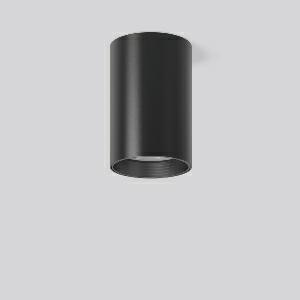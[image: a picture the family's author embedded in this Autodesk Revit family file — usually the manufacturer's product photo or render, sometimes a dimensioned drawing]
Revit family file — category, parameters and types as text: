
# Revit family: heledon_maxi_a_931229_003_1_3319
name_source: partatom
category: Lighting Fixtures
units: mm (PartAtom-declared; Revit-internal decimal feet)

## family parameters
Cut with Voids When Loaded = No
Host = Face
Light Source = No
Part Type = Normal
Room Calculation Point = No
Round Connector Dimension = Use Diameter
Shared = No

## types (1)
- HELEDON maxi A (1 x LED Modul 940, 3800 lm, 4000)
    Apparent Load = 35 VA
    Approval mark = CE
    CIE Flux Codes = 96 100 100 100 100
    Color Rendering = 92
    Color Temperature = 4000
    Default Elevation = 1800 mm
    Description = Series: HELEDON maxi
Cylindrical surface-mounted downlight. Housing: die-cast aluminium, powder-coated. Internal ceiling frame polycarbonate with bayonet mounting. Black plastic ring and recessed LED to prevent glare from the side. Optical assembly with lens made of plastic (polycarbonate) for the best homogeneous light distribution - can be changed without tools. Best colour rendering index Ra>90. Suitable for Ceiling mounting. Easy installation with a separate ceiling frame with bayonet mounting and plug connection. Driver integrated. Connected via plug-in connector. High quality converter without flickering and stroboscopic effect. The following accessories can be mounted without use of tools: interchangeable lenses, decorative glasses, honeycomb louvre, clear and frosted diffusers, white interchangeable plastic ring. 
Colour: deep black, matt (RAL 9005)
Diameter: 123 mm
Height: 183 mm
Lamp: LED
Socket: without socket
Colour temperature: 4000K
Colour rendering index (CRI): 92
System power: 35 W
Rated luminous flux: 3800 lm
Luminous efficiency: 109 lm/W
Control gear: Regulated power supply
Protection class: I
Type of protection: IP 20
    Height = 183 mm
    Lamp = 1 x LED Modul 940
    Lamp Light Flux = 3800 lm
    Lamp count = 1
    Length = 123 mm
    Lifetime = 50000 h
    Luminous efficacy = 109 lm/W
    Manufacturer = RZB
    ModVariant = No
    Model = 931229.003.1
    Mounting Place = Ceiling
    Mounting Type = Surface mounted
    Number of Poles = 1
    OnlyDefault = Yes
    Power Factor = 1
    Product Name = HELEDON maxi A
    Product group = Surface mounted downlights
    ProductGroupID = 302
    Protection Class = Protection class I
    Protection Degree = IP 20
    RLX_Detail_Level = 1
    RLX_Emergency_Light_Flux = 0 lm
    RLX_Emergency_Type = 0
    RLX_Emergency_Type_DB = No
    RlxData = <blob elided: 98605 chars, md5=07a5089c>
    Socket = socket
    Standby Power = 0 W
    System Light Flux = 3800 lm
    System Power = 35 W
    Type Comments = Product without accessories
    Type Image = 931193.003.jpg
    URL = http://relux.com
    VarID = ---
    Voltage = 230 V
    Voltage Range = 220-240 V
    Weight = 0.00 kg
    Width = 0 mm  [stored 0 ft]

note: [stored X ft] marks values corroborated as IEEE doubles in the binary element streams (Revit-internal decimal feet)

## geometry (parser evidence)
native form markers: Blend x4, Sweep x11
no freeform markers — native parametric forms only
